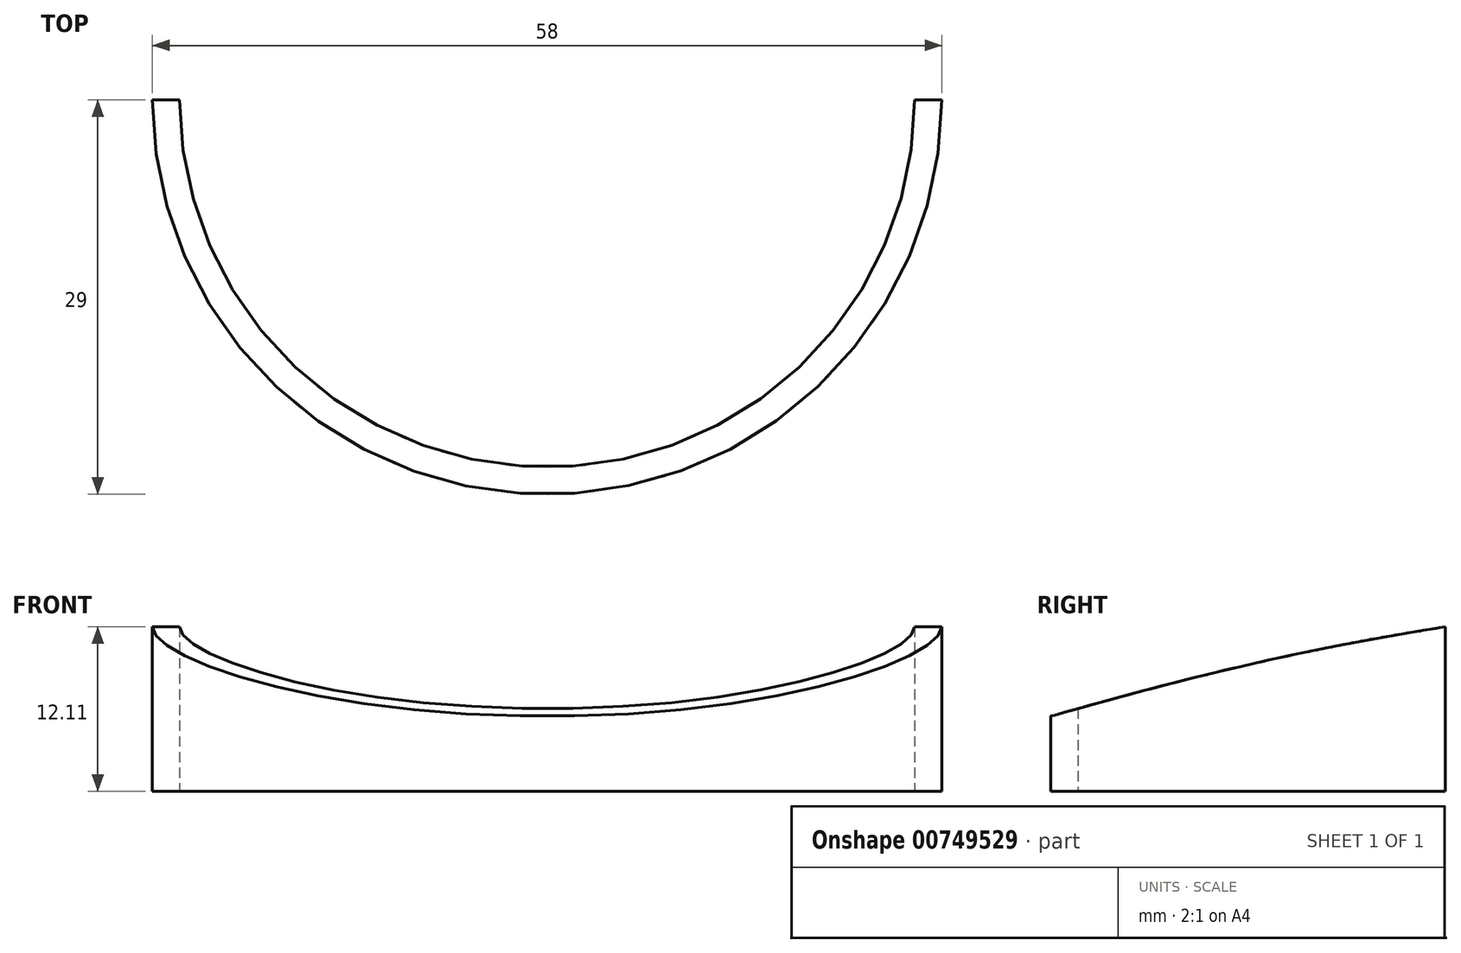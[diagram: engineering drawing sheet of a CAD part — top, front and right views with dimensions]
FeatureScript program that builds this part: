
annotation { "Feature Type Name" : "Feature", "Feature Type Description" : "" }
export const myFeature = defineFeature(function(context is Context, id is Id, definition is map)
    precondition{}
    {
        {
            var Q0;
            Q0=qCreatedBy(makeId("Top.planeOp"),FACE);
            var sketch = newSketch(context, id + "F0", { "sketchPlane" : qUnion([Q0])});
            skArc(sketch, "E0", {"start": v(-29, -45) * mm, "mid": v(0, -74) * mm, "end": v(29, -45) * mm});
            skArc(sketch, "E1.0", {"start": v(-27, -45) * mm, "mid": v(0, -72) * mm, "end": v(27, -45) * mm});
            skLineSegment(sketch, "E2", {"start": v(-29, -45) * mm, "end": v(-27, -45) * mm});
            skLineSegment(sketch, "E3", {"start": v(27, -45) * mm, "end": v(29, -45) * mm});
            skSolve(sketch);
        }
        {
            var Q0;
            Q0=makeQuery(id+"F0.imprint","IMPRINT",FACE,{"disambiguationData":[TD([[makeQuery(id+"F0.imprint","IMPRINT",EDGE,{"derivedFrom":sQuery(id+"F0.wireOp",EDGE,"E0")}),1.0]])]});
            extrude(context, id + "F1", {"entities" : qUnion([Q0]), "depth" : 20 * mm, "offsetDistance" : 25 * mm});
        }
        {
            var Q0;
            Q0=qCreatedBy(makeId("Right.planeOp"),FACE);
            var sketch = newSketch(context, id + "F2", { "sketchPlane" : qUnion([Q0])});
            skFitSpline(sketch, "E4", {"points": [v(-74, 5.54) * mm, v(-57.79, 9.7) * mm, v(-25.23, 14.32) * mm, v(31.25, 12.55) * mm, v(66.54, 4.06) * mm, v(88.88, 0) * mm], "startDerivative": vector(104.05, 29.03) * mm, "endDerivative": vector(127.43, -18.87) * mm});
            skLineSegment(sketch, "E5", {"start": v(88.88, 0) * mm, "end": v(88.88, 32.66) * mm});
            skLineSegment(sketch, "E6", {"start": v(88.88, 32.66) * mm, "end": v(-93.4, 32.66) * mm});
            skLineSegment(sketch, "E7", {"start": v(-93.4, 32.66) * mm, "end": v(-93.4, 5.54) * mm});
            skLineSegment(sketch, "E8", {"start": v(-93.4, 5.54) * mm, "end": v(-74, 5.54) * mm});
            skSolve(sketch);
        }
        {
            var Q0;
            Q0=makeQuery(id+"F2.imprint","IMPRINT",FACE,{"disambiguationData":[TD([[makeQuery(id+"F2.imprint","IMPRINT",EDGE,{"derivedFrom":sQuery(id+"F2.wireOp",EDGE,"E4")}),1.0]])]});
            extrude(context, id + "F3", {"entities" : qUnion([Q0]), "operationType" : NewBodyOperationType.REMOVE, "endBound" : BoundingType.SYMMETRIC, "oppositeDirection" : true, "depth" : 100 * mm, "offsetDistance" : 25 * mm});
        }
    });
